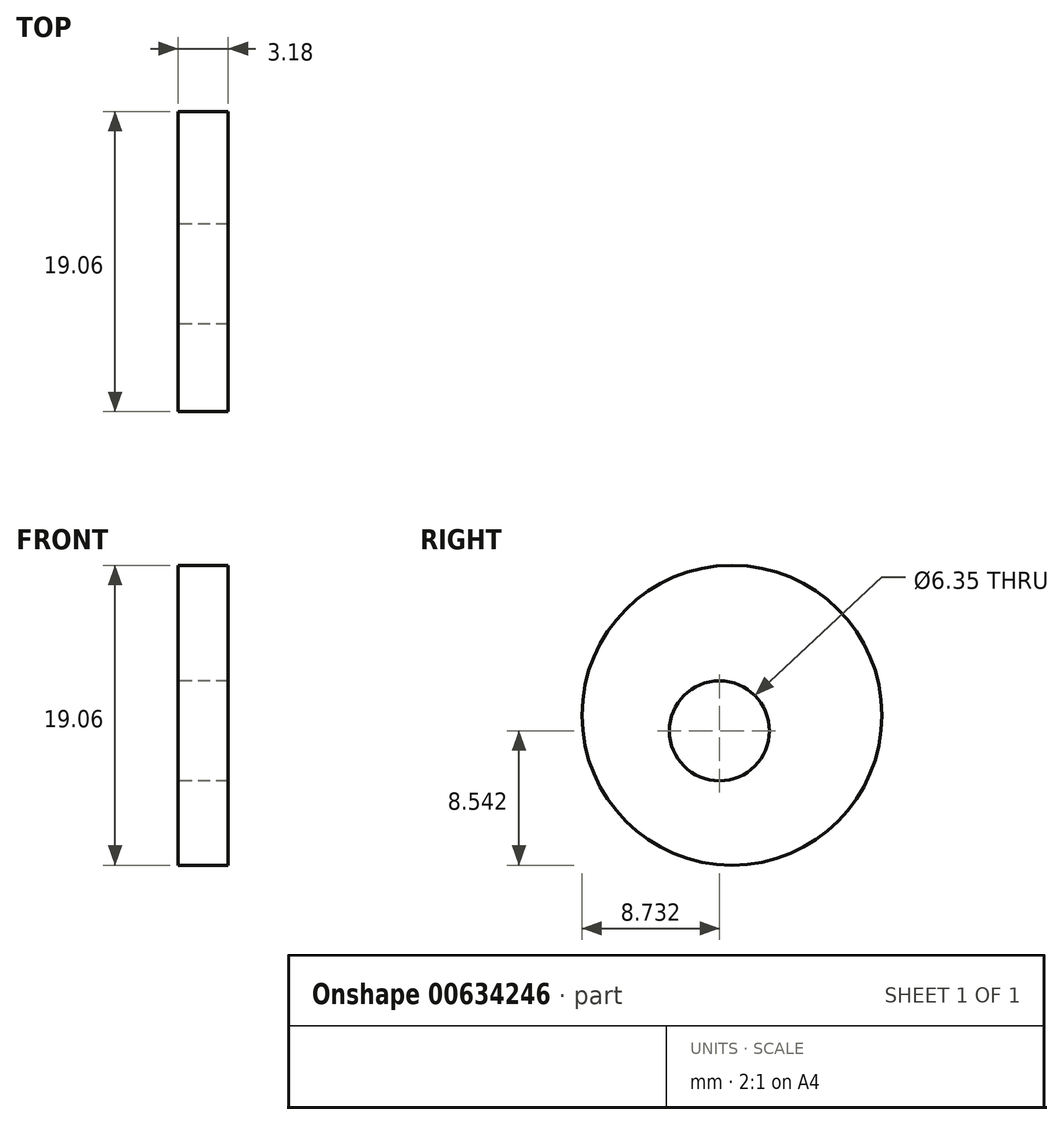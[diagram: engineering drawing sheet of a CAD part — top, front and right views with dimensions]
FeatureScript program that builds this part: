
annotation { "Feature Type Name" : "Feature", "Feature Type Description" : "" }
export const myFeature = defineFeature(function(context is Context, id is Id, definition is map)
    precondition{}
    {
        {
            var Q0;
            Q0=qCreatedBy(makeId("Right.planeOp"),FACE);
            var sketch = newSketch(context, id + "F0", { "sketchPlane" : qUnion([Q0])});
            skCircle(sketch, "E0", {"center": v(0, 0) * mm, "radius": 9.53 * mm});
            skCircle(sketch, "E1", {"center": v(-0.8, -0.99) * mm, "radius": 3.18 * mm});
            skSolve(sketch);
        }
        {
            var Q0;
            Q0 = qSketchRegion(id + "F0", true);
            extrude(context, id + "F1", {"entities" : qUnion([Q0]), "depth" : 3.17 * mm, "offsetDistance" : 25.4 * mm});
        }
    });
